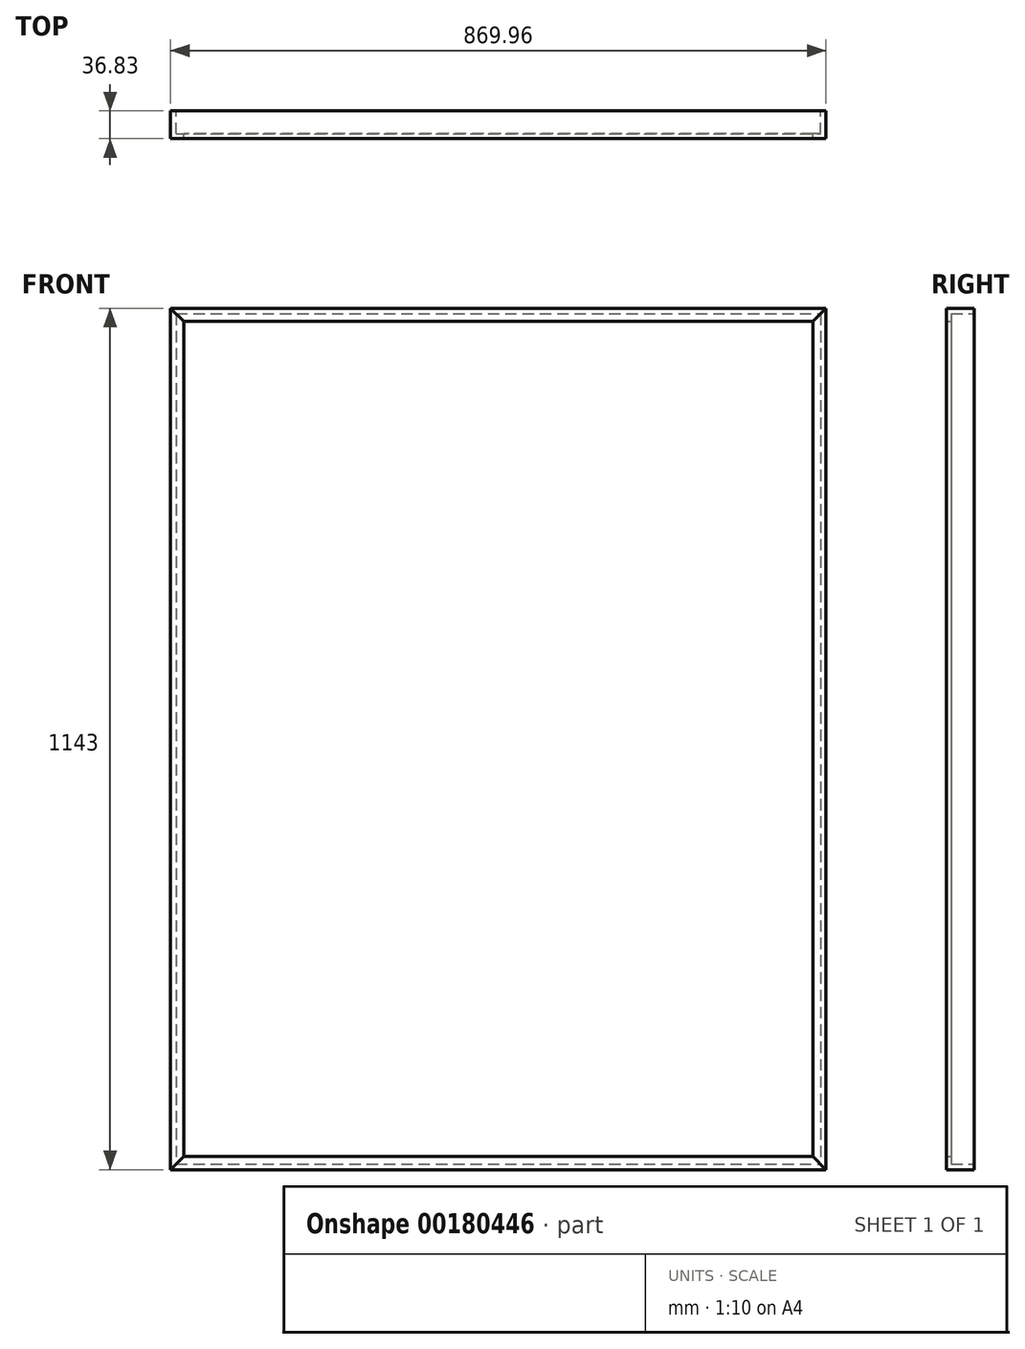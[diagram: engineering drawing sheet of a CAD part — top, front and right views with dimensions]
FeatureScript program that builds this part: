
annotation { "Feature Type Name" : "Feature", "Feature Type Description" : "" }
export const myFeature = defineFeature(function(context is Context, id is Id, definition is map)
    precondition{}
    {
        {
            var Q0;
            Q0=qCreatedBy(makeId("Front.planeOp"),FACE);
            var sketch = newSketch(context, id + "F0", { "sketchPlane" : qUnion([Q0])});
            skLineSegment(sketch, "E0.bottom", {"start": v(-434.98, -571.5) * mm, "end": v(434.98, -571.5) * mm});
            skLineSegment(sketch, "E0.top", {"start": v(-434.98, 571.5) * mm, "end": v(434.98, 571.5) * mm});
            skLineSegment(sketch, "E0.left", {"start": v(-434.98, -571.5) * mm, "end": v(-434.98, 571.5) * mm});
            skLineSegment(sketch, "E0.right", {"start": v(434.98, -571.5) * mm, "end": v(434.98, 571.5) * mm});
            skPoint(sketch, "E0.middle", {"position": v(0, 0) * mm});
            skLineSegment(sketch, "E1.bottom", {"start": v(417.58, 554.1) * mm, "end": v(-417.58, 554.1) * mm});
            skLineSegment(sketch, "E1.top", {"start": v(417.58, -554.1) * mm, "end": v(-417.58, -554.1) * mm});
            skLineSegment(sketch, "E1.left", {"start": v(417.58, 554.1) * mm, "end": v(417.58, -554.1) * mm});
            skLineSegment(sketch, "E1.right", {"start": v(-417.58, 554.1) * mm, "end": v(-417.58, -554.1) * mm});
            skSolve(sketch);
        }
        {
            var Q0;
            Q0=makeQuery(id+"F0.imprint","IMPRINT",FACE,{"disambiguationData":[TD([[makeQuery(id+"F0.imprint","IMPRINT",EDGE,{"derivedFrom":sQuery(id+"F0.wireOp",EDGE,"E1.bottom")}),1.0]])]});
            var sketch = newSketch(context, id + "F1", { "sketchPlane" : qUnion([Q0])});
            skLineSegment(sketch, "E2.0", {"start": v(-434.98, -571.5) * mm, "end": v(-434.98, 571.5) * mm});
            skLineSegment(sketch, "E3.0", {"start": v(434.98, -571.5) * mm, "end": v(434.98, 571.5) * mm});
            skLineSegment(sketch, "E4.0", {"start": v(-417.58, 554.1) * mm, "end": v(-417.58, -554.1) * mm});
            skLineSegment(sketch, "E5.0", {"start": v(417.58, 554.1) * mm, "end": v(417.58, -554.1) * mm});
            skLineSegment(sketch, "E6", {"start": v(-434.98, 571.5) * mm, "end": v(-417.58, 554.1) * mm});
            skLineSegment(sketch, "E7", {"start": v(434.98, 571.5) * mm, "end": v(417.58, 554.1) * mm});
            skLineSegment(sketch, "E8", {"start": v(-417.58, -554.1) * mm, "end": v(-434.98, -571.5) * mm});
            skLineSegment(sketch, "E9", {"start": v(417.58, -554.1) * mm, "end": v(434.98, -571.5) * mm});
            skSolve(sketch);
        }
        {
            var Q0;
            Q0 = qSketchRegion(id + "F1", true);
            extrude(context, id + "F2", {"entities" : qUnion([Q0]), "depth" : 36.83 * mm});
        }
        {
            var Q0;
            Q0=qCreatedBy(makeId("Front.planeOp"),FACE);
            var sketch = newSketch(context, id + "F3", { "sketchPlane" : qUnion([Q0])});
            skLineSegment(sketch, "E10.0", {"start": v(-434.98, 571.5) * mm, "end": v(434.98, 571.5) * mm});
            skLineSegment(sketch, "E11.0", {"start": v(417.58, 554.1) * mm, "end": v(-417.58, 554.1) * mm});
            skLineSegment(sketch, "E12.0", {"start": v(-434.98, 571.5) * mm, "end": v(-417.58, 554.1) * mm});
            skLineSegment(sketch, "E13.0", {"start": v(434.98, 571.5) * mm, "end": v(417.58, 554.1) * mm});
            skLineSegment(sketch, "E14.0", {"start": v(-434.98, -571.5) * mm, "end": v(434.98, -571.5) * mm});
            skLineSegment(sketch, "E15.0", {"start": v(417.58, -554.1) * mm, "end": v(-417.58, -554.1) * mm});
            skLineSegment(sketch, "E16.0", {"start": v(-417.58, -554.1) * mm, "end": v(-434.98, -571.5) * mm});
            skLineSegment(sketch, "E17.0", {"start": v(417.58, -554.1) * mm, "end": v(434.98, -571.5) * mm});
            skSolve(sketch);
        }
        {
            var Q0;
            Q0 = qSketchRegion(id + "F3", true);
            var Q1;
            Q1=makeQuery(id+"F2.opExtrude","CAP_FACE",FACE,{"disambiguationData":[OSD([sQuery(id+"F1.wireOp",EDGE,"E2.0"),sQuery(id+"F1.wireOp",EDGE,"E4.0"),sQuery(id+"F1.wireOp",EDGE,"E6"),sQuery(id+"F1.wireOp",EDGE,"E8")])],"isStart":false});
            extrude(context, id + "F4", {"entities" : qUnion([Q0]), "endBound" : BoundingType.UP_TO_SURFACE, "endBoundEntityFace" : qUnion([Q1]), "depth" : 25.4 * mm});
        }
        {
            var Q0;
            Q0=makeQuery(id+"F0.imprint","IMPRINT",FACE,{"disambiguationData":[TD([[makeQuery(id+"F0.imprint","IMPRINT",EDGE,{"derivedFrom":sQuery(id+"F0.wireOp",EDGE,"E0.bottom")}),1.0]])]});
            var sketch = newSketch(context, id + "F5", { "sketchPlane" : qUnion([Q0])});
            skLineSegment(sketch, "E18.bottom", {"start": v(-427.74, 564.26) * mm, "end": v(427.74, 564.26) * mm});
            skLineSegment(sketch, "E18.top", {"start": v(-427.74, -564.26) * mm, "end": v(427.74, -564.26) * mm});
            skLineSegment(sketch, "E18.left", {"start": v(-427.74, 564.26) * mm, "end": v(-427.74, -564.26) * mm});
            skLineSegment(sketch, "E18.right", {"start": v(427.74, 564.26) * mm, "end": v(427.74, -564.26) * mm});
            skPoint(sketch, "E18.middle", {"position": v(0, 0) * mm});
            skSolve(sketch);
        }
        {
            var Q0;
            Q0 = qSketchRegion(id + "F5", true);
            extrude(context, id + "F6", {"entities" : qUnion([Q0]), "operationType" : NewBodyOperationType.REMOVE, "depth" : 30.48 * mm});
        }
    });
